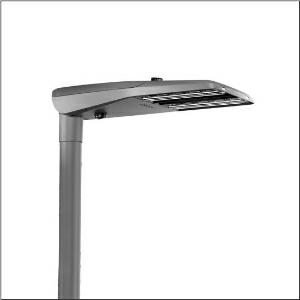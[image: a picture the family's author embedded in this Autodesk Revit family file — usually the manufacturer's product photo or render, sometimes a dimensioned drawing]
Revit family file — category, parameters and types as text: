
# Revit family: streetlight_sl_11_iq_midi___st1_2a_5xc3a41y08le_52ec
name_source: partatom
category: Lighting Fixtures
units: mm (PartAtom-declared; Revit-internal decimal feet)

## family parameters
Cut with Voids When Loaded = No
Host = Face
Light Source = No
Part Type = Normal
Room Calculation Point = No
Round Connector Dimension = Use Diameter
Shared = No

## types (1)
- --- (1 x LED, 9590 lm, 59.4 W, 4000K)
    Apparent Load = 59 VA
    CIE Flux Codes = 32 70 96 100 100
    Color Rendering = 70
    Color Temperature = 4000K
    Default Elevation = 1800 mm
    Description = Streetlight SL 11 iQ midi, mast luminaire, primary light control with 3 zone facetted reflector, of plastic, silver coated, highly specular, primary optical cover: cover, of PMMA, transparent, light distribution: ST1.2a, light emission: direct distribution, primary light characteristic: asymmetric, installation type: post-top, side-entry, LED, High Power LED, rated luminous flux: 9.590lm, luminous efficacy: 163lm/W, light colour: 740, colour temperature: 4000K, control: presetting dimming logarithmic, Street-Remote, Auto-Match, Temp-Guard, Lumen-Switch, Night-Set, Smart-Wire, Light-Fading, Desk-Remote (wireless, voltage-free reading and setting of iQ features in the workshop via application-optimized NFC function/RFID function), optimised constant luminous flux control (CLO 2.0), with cable H07RN-F 5x 1.5mm², mains connection: 220..240V, AC, 50/60Hz, connection cable pre-assembled, cable length: 8,5m, start of lifetime: 59W, end of service life: 62W, reduction: 29W, luminaire housing, of diecast aluminium, powder-coated, Siteco® metallic grey (DB 702S), please order mast flange separately, inclination adjustable without tools: 0°, 5°, 10°, 15° (post-top) | 0°, -5°, -10°, -15° (side-entry), sealing non-destructively replaceable, multi-level sealing system, length: 780mm, width: 376mm, height: 118mm, spigot size: 60/76mm (post-top) and 42/60/76mm (side-entry), mast flange for spigot size: 42mm: 5XC10008XM4, 60mm: 5XC10008XM2, 76/60mm: 5XC10108XM1, equipment: standard, Smart Interface below and above, protection rating (complete): IP66, insulation class (complete): insulation class II (safety insulation), certification: CE, ENEC in preparation, impact resistance: IK09, permissible operating ambient temperature for outdoor applications: -25..+50°C, standard-compliant lighting for roads and squares, packaging unit: 1 piece

Light Distribution: ST1.2a
    Height = 118 mm
    Lamp = 1 x LED
    Lamp Light Flux = 9590 lm
    Lamp Power = 59.4 W
    Lamp count = 1
    Length = 780 mm
    Luminous efficacy = 161 lm/W
    Manufacturer = Siteco
    ModVariant = No
    Model = 5XC3A41Y08LE
    Number of Poles = 1
    OnlyDefault = Yes
    Power Factor = 1
    Product Name = Streetlight SL 11 iQ midi | ST1.2a
    Product group = mast luminaire | pylon top
    ProductGroupID = 6100
    Protection Class = Protection class II
    Protection Degree = IP 66
    RLX_Detail_Level = 1
    RlxData = <blob elided: 69581 chars, md5=594bc8d0>
    Socket = socket
    Standby Power = 0 W
    System Light Flux = 9590 lm
    System Power = 59 W
    Type Comments = factory setting: luminous flux: 100 % | dim-lin: 254 | 521 mA
    Type Image = l_1004429.jpg
    URL = http://relux.com
    VarID = @adj_043619
    Voltage = 0 V
    Weight = 0.00 kg
    Width = 376 mm

## geometry (parser evidence)
native form markers: Blend x4, Sweep x10
no freeform markers — native parametric forms only
